# Revit family: MR_ОсветительныйПрибор_Cube
name_source: partatom
category: Осветительные приборы
units: mm (PartAtom-declared; Revit-internal decimal feet)

## family parameters
Всегда вертикально = Да
Источник света = Да
На основе рабочей плоскости = Да
Общий = Да
При загрузке вырезать с полостями = Нет
Размер круглого соединителя = Использовать диаметр
Тип детали = Нормальный
Точка расчета площади = Нет

## types (4) — shared parameters
ADSK_URL страницы изделия = https://martinirus.ru
ADSK_Группирование = Наружное освещение_светильник
ADSK_Единица измерения = шт.
ADSK_Завод-изготовитель = MartiniRUS
ADSK_Классификация нагрузок = Освещение
ADSK_Количество = 1
ADSK_Количество фаз = 1
ADSK_Количество фаз числовое = 1
ADSK_Коэффициент мощности = 0.98
ADSK_Материал = <По категории>
ADSK_Напряжение = 230 В
ADSK_Ток = 0 А
IP Class = IP65
Видимая форма излучения при визуализации = Да
Группа модели = Cube
Излучение по диаметру окружности = 80 мм
Класс Защиты = I
Климатическая зона = УХЛ1
Описание = Cube
Отметка по умолчанию = 1219 мм
Самосветящий материал = Источник света по умолчанию
Светофильтр = 16777215
Смещение цветовой температуры при затухании лампы = <Нет>
Угол наклона = 90.00°

## per-type parameters (varying)
| type | ADSK_Код изделия | ADSK_Масса | ADSK_Номинальная мощность | ADSK_Полная мощность | ADSK_Размер_Высота | ВысотаОснования | Полная установленная мощность | Файл фотометрической сетки |
| Cube_26w_3000mm_3000k | P864424__WW | 16.8 | 26 Вт | 27 В·А | 3000 мм | 697 мм | 27 В·А | P864424NCWW.ies |
| Cube_26w_3000mm_4000k | P864424__NW | 16.8 | 26 Вт | 27 В·А | 3000 мм | 697 мм | 27 В·А | P864424NCNW.ies |
| Cube_13w_1000mm_4000k | P864423__NW | 7.8 | 13 Вт | 13 В·А | 1000 мм | 247 мм | 13 В·А | P864423NCNW.ies |
| Cube_13w_1000mm_3000k | P864423__WW | 7.8 | 13 Вт | 13 В·А | 1000 мм | 247 мм | 13 В·А | P864423NCWW.ies |

note: column(s) folded — value = type name in every type: ADSK_Наименование
